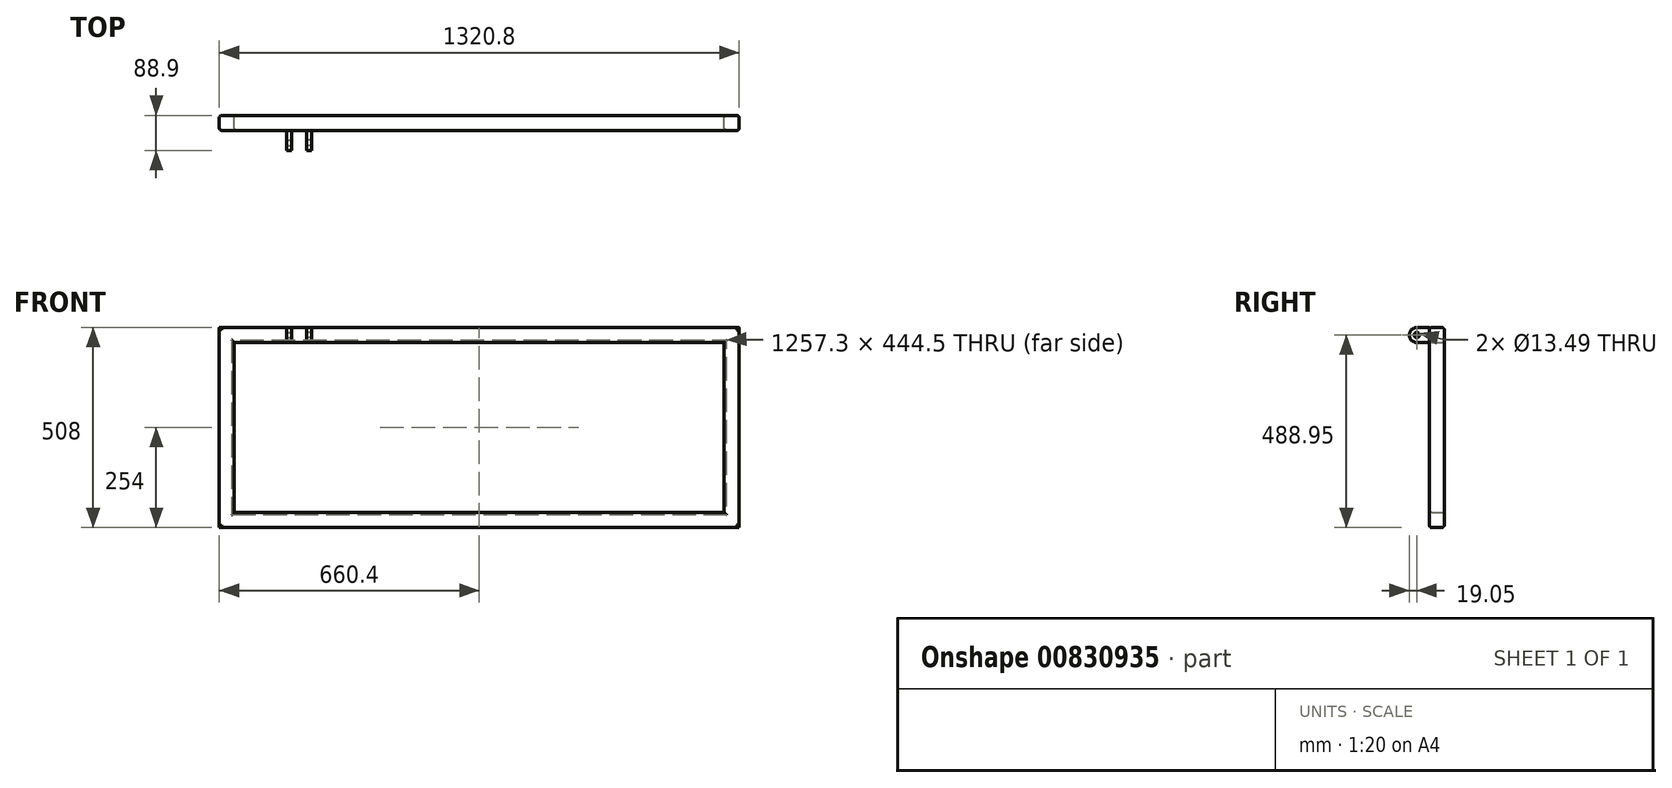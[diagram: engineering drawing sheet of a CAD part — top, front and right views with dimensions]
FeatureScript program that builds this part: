
annotation { "Feature Type Name" : "Feature", "Feature Type Description" : "" }
export const myFeature = defineFeature(function(context is Context, id is Id, definition is map)
    precondition{}
    {
        {
            var Q0;
            Q0=qCreatedBy(makeId("Front.planeOp"),FACE);
            var sketch = newSketch(context, id + "F0", { "sketchPlane" : qUnion([Q0])});
            skLineSegment(sketch, "E0.bottom", {"start": v(-660.4, 254) * mm, "end": v(660.4, 254) * mm});
            skLineSegment(sketch, "E0.top", {"start": v(-660.4, -254) * mm, "end": v(660.4, -254) * mm});
            skLineSegment(sketch, "E0.left", {"start": v(-660.4, 254) * mm, "end": v(-660.4, -254) * mm});
            skLineSegment(sketch, "E0.right", {"start": v(660.4, 254) * mm, "end": v(660.4, -254) * mm});
            skPoint(sketch, "E0.middle", {"position": v(0, 0) * mm});
            skLineSegment(sketch, "E1.bottom", {"start": v(-622.3, 215.9) * mm, "end": v(622.3, 215.9) * mm});
            skLineSegment(sketch, "E1.top", {"start": v(-622.3, -215.9) * mm, "end": v(622.3, -215.9) * mm});
            skLineSegment(sketch, "E1.left", {"start": v(-622.3, 215.9) * mm, "end": v(-622.3, -215.9) * mm});
            skLineSegment(sketch, "E1.right", {"start": v(622.3, 215.9) * mm, "end": v(622.3, -215.9) * mm});
            skSolve(sketch);
        }
        {
            var Q0;
            Q0 = qSketchRegion(id + "F0", true);
            extrude(context, id + "F1", {"entities" : qUnion([Q0]), "depth" : 38.1 * mm, "offsetDistance" : 25.4 * mm});
        }
        {
            var Q0;
            Q0=makeQuery(id+"F1.opExtrude","CAP_FACE",FACE,{"disambiguationData":[OSD([sQuery(id+"F0.wireOp",EDGE,"E0.bottom"),sQuery(id+"F0.wireOp",EDGE,"E0.top"),sQuery(id+"F0.wireOp",EDGE,"E0.left"),sQuery(id+"F0.wireOp",EDGE,"E0.right"),sQuery(id+"F0.wireOp",EDGE,"E1.bottom"),sQuery(id+"F0.wireOp",EDGE,"E1.top"),sQuery(id+"F0.wireOp",EDGE,"E1.left"),sQuery(id+"F0.wireOp",EDGE,"E1.right")])],"isStart":false});
            var Q1;
            Q1=makeQuery(id+"F1.opExtrude","CAP_FACE",FACE,{"disambiguationData":[OSD([sQuery(id+"F0.wireOp",EDGE,"E0.bottom"),sQuery(id+"F0.wireOp",EDGE,"E0.top"),sQuery(id+"F0.wireOp",EDGE,"E0.left"),sQuery(id+"F0.wireOp",EDGE,"E0.right"),sQuery(id+"F0.wireOp",EDGE,"E1.bottom"),sQuery(id+"F0.wireOp",EDGE,"E1.top"),sQuery(id+"F0.wireOp",EDGE,"E1.left"),sQuery(id+"F0.wireOp",EDGE,"E1.right")])],"isStart":true});
            fillet(context, id + "F2", {"entities" : qUnion([Q0, Q1]), "radius" : 6.35 * mm, "tangentPropagation" : true, "allowEdgeOverflow" : false});
        }
        {
            var Q0;
            Q0=makeQuery(id+"F1.opExtrude","CAP_FACE",FACE,{"disambiguationData":[OSD([sQuery(id+"F0.wireOp",EDGE,"E0.bottom"),sQuery(id+"F0.wireOp",EDGE,"E0.top"),sQuery(id+"F0.wireOp",EDGE,"E0.left"),sQuery(id+"F0.wireOp",EDGE,"E0.right"),sQuery(id+"F0.wireOp",EDGE,"E1.bottom"),sQuery(id+"F0.wireOp",EDGE,"E1.top"),sQuery(id+"F0.wireOp",EDGE,"E1.left"),sQuery(id+"F0.wireOp",EDGE,"E1.right")])],"isStart":false});
            var sketch = newSketch(context, id + "F3", { "sketchPlane" : qUnion([Q0])});
            skLineSegment(sketch, "E2", {"start": v(0, 348.54) * mm, "end": v(0, -363.27) * mm, "construction": true});
            skLineSegment(sketch, "E3.0", {"start": v(-457.2, 348.54) * mm, "end": v(-457.2, -363.27) * mm, "construction": true});
            skLineSegment(sketch, "E4", {"start": v(-762.77, 0) * mm, "end": v(738.46, 0) * mm, "construction": true});
            skLineSegment(sketch, "E5.0", {"start": v(-476.25, 348.54) * mm, "end": v(-476.25, -363.27) * mm, "construction": true});
            skLineSegment(sketch, "E6.0", {"start": v(-660.4, 254) * mm, "end": v(660.4, 254) * mm, "construction": true});
            skLineSegment(sketch, "E7.bottom", {"start": v(-476.25, 254) * mm, "end": v(-488.95, 254) * mm});
            skLineSegment(sketch, "E7.top", {"start": v(-476.25, 215.9) * mm, "end": v(-488.95, 215.9) * mm});
            skLineSegment(sketch, "E7.left", {"start": v(-476.25, 254) * mm, "end": v(-476.25, 215.9) * mm});
            skLineSegment(sketch, "E7.right", {"start": v(-488.95, 254) * mm, "end": v(-488.95, 215.9) * mm});
            skSolve(sketch);
        }
        {
            var Q0;
            Q0 = qSketchRegion(id + "F3", true);
            extrude(context, id + "F4", {"entities" : qUnion([Q0]), "depth" : 50.8 * mm, "offsetDistance" : 25.4 * mm});
        }
        {
            var Q0;
            Q0=makeQuery(id+"F4.opExtrude","CAP_EDGE",EDGE,{"disambiguationData":[OSD([sQuery(id+"F3.wireOp",EDGE,"E7.bottom")])],"isStart":false});
            var Q1;
            Q1=makeQuery(id+"F4.opExtrude","CAP_EDGE",EDGE,{"disambiguationData":[OSD([sQuery(id+"F3.wireOp",EDGE,"E7.top")])],"isStart":false});
            fillet(context, id + "F5", {"entities" : qUnion([Q0, Q1]), "radius" : 19.05 * mm, "tangentPropagation" : true, "allowEdgeOverflow" : false});
        }
        {
            var Q0;
            Q0=makeQuery(id+"F4.opExtrude","SWEPT_FACE",FACE,{"disambiguationData":[OSD([sQuery(id+"F3.wireOp",EDGE,"E7.left")])]});
            var sketch = newSketch(context, id + "F6", { "sketchPlane" : qUnion([Q0])});
            skArc(sketch, "E8.0", {"start": v(-69.85, 254) * mm, "mid": v(-88.9, 234.95) * mm, "end": v(-69.85, 215.9) * mm, "construction": true});
            skSolve(sketch);
        }
        {
            var Q0;
            Q0=sQuery(id+"F6.wireOp",VERTEX,"E8.0.center");
            var Q1;
            Q1=makeQuery(id+"F4.opExtrude","SWEPT_BODY",BODY,{"disambiguationData":[OSD([sQuery(id+"F3.wireOp",EDGE,"E7.bottom"),sQuery(id+"F3.wireOp",EDGE,"E7.top"),sQuery(id+"F3.wireOp",EDGE,"E7.left"),sQuery(id+"F3.wireOp",EDGE,"E7.right")])]});
            hole(context, id + "F7", {"style" : HoleStyle.SIMPLE, "endStyle" : HoleEndStyle.THROUGH, "standardTappedOrClearance" : lookupTablePath({ "fit" : "Normal (ASME)", "standard" : "ANSI", "size" : "1/2", "type" : "Clearance" }), "standardBlindInLast" : lookupTablePath({ "fit" : "Free", "standard" : "ANSI", "size" : "1/2", "type" : "Clearance" }), "holeDiameter" : 13.5 * mm, "majorDiameter" : 6.35 * mm, "isTappedThrough" : true, "tappedDepth" : 38.1 * mm, "tapClearance" : 3, "startFromSketch" : true, "locations" : qUnion([Q0]), "scope" : qUnion([Q1])});
        }
        {
            var Q0;
            Q0=makeQuery(id+"F4.opExtrude","SWEPT_FACE",FACE,{"disambiguationData":[OSD([sQuery(id+"F3.wireOp",EDGE,"E7.left")])]});
            cPlane(context, id + "F8", {"entities" : qUnion([Q0]), "cplaneType" : CPlaneType.OFFSET, "offset" : 19.05 * mm, "width" : 152.4 * mm, "height" : 152.4 * mm});
        }
        {
            var Q0;
            Q0=makeQuery(id+"F4.opExtrude","SWEPT_BODY",BODY,{"disambiguationData":[OSD([sQuery(id+"F3.wireOp",EDGE,"E7.bottom"),sQuery(id+"F3.wireOp",EDGE,"E7.top"),sQuery(id+"F3.wireOp",EDGE,"E7.left"),sQuery(id+"F3.wireOp",EDGE,"E7.right")])]});
            var Q1;
            Q1=qCreatedBy(id+"F8.planeOp",FACE);
            mirror(context, id + "F9", {"entities" : qUnion([Q0]), "mirrorPlane" : qUnion([Q1])});
        }
    });
